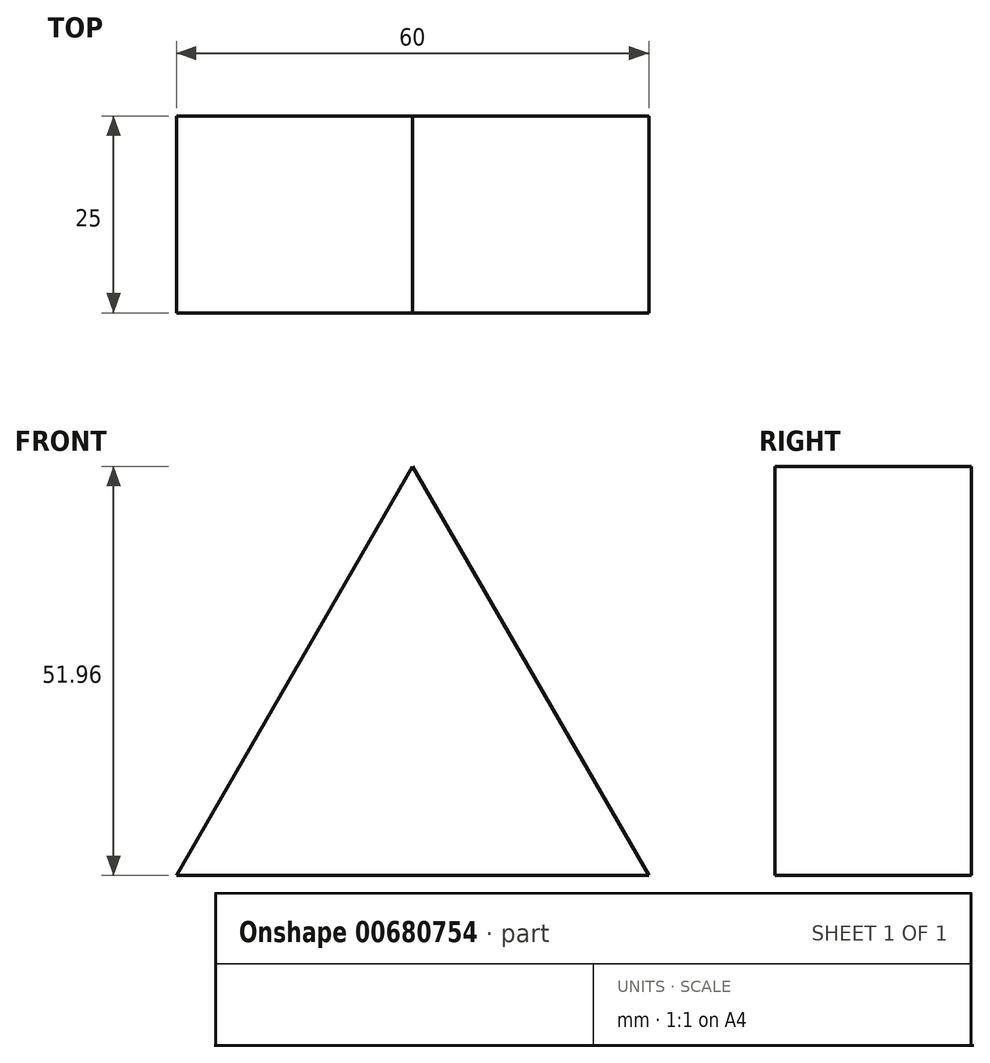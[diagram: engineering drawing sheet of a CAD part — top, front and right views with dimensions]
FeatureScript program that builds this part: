
annotation { "Feature Type Name" : "Feature", "Feature Type Description" : "" }
export const myFeature = defineFeature(function(context is Context, id is Id, definition is map)
    precondition{}
    {
        {
            var Q0;
            Q0=qCreatedBy(makeId("Front.planeOp"),FACE);
            var sketch = newSketch(context, id + "F0", { "sketchPlane" : qUnion([Q0])});
            skLineSegment(sketch, "E0", {"start": v(0, 0) * mm, "end": v(30, 0) * mm});
            skLineSegment(sketch, "E1", {"start": v(0, 0) * mm, "end": v(-30, 0) * mm});
            skLineSegment(sketch, "E2", {"start": v(-30, 0) * mm, "end": v(0, 51.96) * mm});
            skLineSegment(sketch, "E3", {"start": v(0, 51.96) * mm, "end": v(30, 0) * mm});
            skSolve(sketch);
        }
        {
            var Q0;
            Q0=makeQuery(id+"F0.imprint","IMPRINT",FACE,{"disambiguationData":[TD([[makeQuery(id+"F0.imprint","IMPRINT",EDGE,{"derivedFrom":sQuery(id+"F0.wireOp",EDGE,"E0")}),1.0]])]});
            extrude(context, id + "F1", {"entities" : qUnion([Q0]), "depth" : 25 * mm, "offsetDistance" : 25 * mm});
        }
    });
